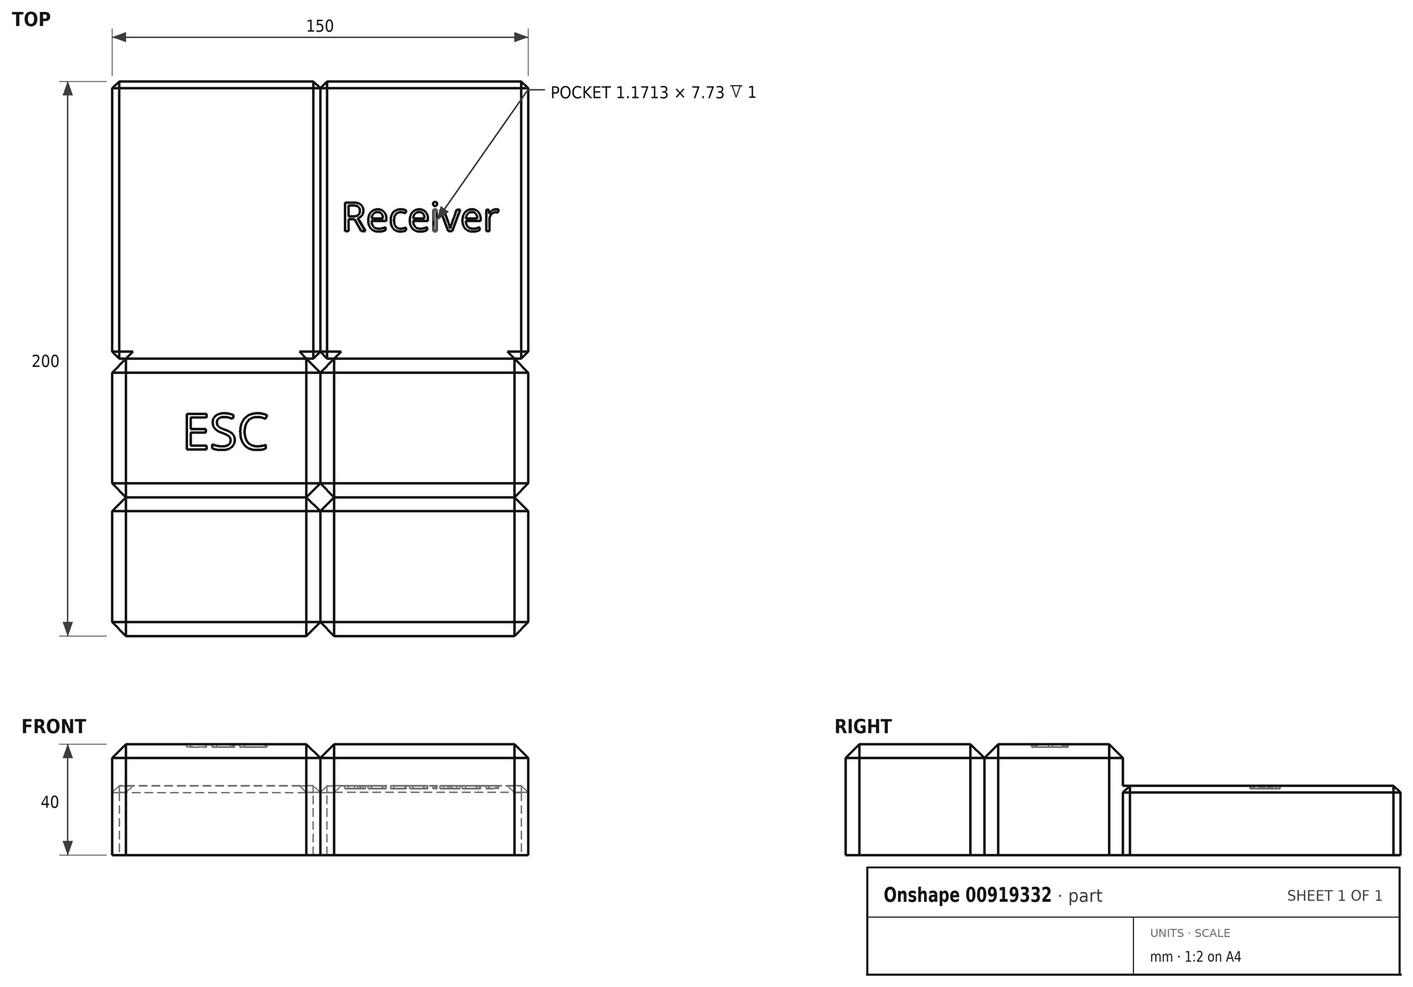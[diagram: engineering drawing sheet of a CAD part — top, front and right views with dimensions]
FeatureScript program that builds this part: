
annotation { "Feature Type Name" : "Feature", "Feature Type Description" : "" }
export const myFeature = defineFeature(function(context is Context, id is Id, definition is map)
    precondition{}
    {
        {
            var Q0;
            Q0=qCreatedBy(makeId("Top.planeOp"),FACE);
            var sketch = newSketch(context, id + "F0", { "sketchPlane" : qUnion([Q0])});
            skLineSegment(sketch, "E0.bottom", {"start": v(0, 0) * mm, "end": v(75, 0) * mm});
            skLineSegment(sketch, "E0.top", {"start": v(0, 50) * mm, "end": v(75, 50) * mm});
            skLineSegment(sketch, "E0.left", {"start": v(0, 0) * mm, "end": v(0, 50) * mm});
            skLineSegment(sketch, "E0.right", {"start": v(75, 0) * mm, "end": v(75, 50) * mm});
            skSolve(sketch);
        }
        {
            var Q0;
            Q0=makeQuery(id+"F0.imprint","IMPRINT",FACE,{"disambiguationData":[TD([[makeQuery(id+"F0.imprint","IMPRINT",EDGE,{"derivedFrom":sQuery(id+"F0.wireOp",EDGE,"E0.bottom")}),1.0]])]});
            extrude(context, id + "F1", {"entities" : qUnion([Q0]), "depth" : 40 * mm, "offsetDistance" : 25 * mm});
        }
        {
            var Q0;
            Q0=makeQuery(id+"F1.opExtrude","SWEPT_EDGE",EDGE,{"disambiguationData":[OSD([sQuery(id+"F0.wireOp",EDGE,"E0.bottom"),sQuery(id+"F0.wireOp",EDGE,"E0.left")])]});
            var Q1;
            Q1=makeQuery(id+"F1.opExtrude","SWEPT_EDGE",EDGE,{"disambiguationData":[OSD([sQuery(id+"F0.wireOp",EDGE,"E0.bottom"),sQuery(id+"F0.wireOp",EDGE,"E0.right")])]});
            var Q2;
            Q2=makeQuery(id+"F1.opExtrude","SWEPT_EDGE",EDGE,{"disambiguationData":[OSD([sQuery(id+"F0.wireOp",EDGE,"E0.top"),sQuery(id+"F0.wireOp",EDGE,"E0.right")])]});
            var Q3;
            Q3=makeQuery(id+"F1.opExtrude","SWEPT_EDGE",EDGE,{"disambiguationData":[OSD([sQuery(id+"F0.wireOp",EDGE,"E0.top"),sQuery(id+"F0.wireOp",EDGE,"E0.left")])]});
            var Q4;
            Q4=makeQuery(id+"F1.opExtrude","CAP_FACE",FACE,{"disambiguationData":[OSD([sQuery(id+"F0.wireOp",EDGE,"E0.bottom"),sQuery(id+"F0.wireOp",EDGE,"E0.top"),sQuery(id+"F0.wireOp",EDGE,"E0.left"),sQuery(id+"F0.wireOp",EDGE,"E0.right")])],"isStart":false});
            chamfer(context, id + "F2", {"entities" : qUnion([Q0, Q1, Q2, Q3, Q4]), "width" : 5 * mm, "tangentPropagation" : true});
        }
        {
            var Q0;
            Q0=makeQuery(id+"F1.opExtrude","SWEPT_BODY",BODY,{"disambiguationData":[OSD([sQuery(id+"F0.wireOp",EDGE,"E0.bottom"),sQuery(id+"F0.wireOp",EDGE,"E0.top"),sQuery(id+"F0.wireOp",EDGE,"E0.left"),sQuery(id+"F0.wireOp",EDGE,"E0.right")])]});
            var Q1;
            Q1=makeQuery(id+"F1.opExtrude","SWEPT_FACE",FACE,{"disambiguationData":[OSD([sQuery(id+"F0.wireOp",EDGE,"E0.top")])]});
            mirror(context, id + "F3", {"operationType" : NewBodyOperationType.ADD, "entities" : qUnion([Q0]), "mirrorPlane" : qUnion([Q1])});
        }
        {
            var Q0;
            {var subQ0=makeQuery(id+"F1.opExtrude","CAP_FACE",FACE,{"disambiguationData":[OSD([sQuery(id+"F0.wireOp",EDGE,"E0.bottom"),sQuery(id+"F0.wireOp",EDGE,"E0.top"),sQuery(id+"F0.wireOp",EDGE,"E0.left"),sQuery(id+"F0.wireOp",EDGE,"E0.right")])],"isStart":true});Q0=makeQuery(id+"F3.boolean.opBoolean","MERGE",FACE,{"derivedFrom":[subQ0,makeQuery(id+"F3.opPattern","COPY",FACE,{"derivedFrom":subQ0,"instanceName":"1"})]});}
            var sketch = newSketch(context, id + "F4", { "sketchPlane" : qUnion([Q0])});
            skLineSegment(sketch, "E1.bottom", {"start": v(0, -100) * mm, "end": v(75, -100) * mm});
            skLineSegment(sketch, "E1.top", {"start": v(0, -200) * mm, "end": v(75, -200) * mm});
            skLineSegment(sketch, "E1.left", {"start": v(0, -100) * mm, "end": v(0, -200) * mm});
            skLineSegment(sketch, "E1.right", {"start": v(75, -100) * mm, "end": v(75, -200) * mm});
            skSolve(sketch);
        }
        {
            var Q0;
            Q0=makeQuery(id+"F4.imprint","IMPRINT",FACE,{"disambiguationData":[TD([[makeQuery(id+"F4.imprint","IMPRINT",EDGE,{"derivedFrom":sQuery(id+"F4.wireOp",EDGE,"E1.top")}),1.0]])]});
            extrude(context, id + "F5", {"entities" : qUnion([Q0]), "operationType" : NewBodyOperationType.ADD, "oppositeDirection" : true, "depth" : 25 * mm, "offsetDistance" : 25 * mm});
        }
        {
            var Q0;
            Q0=makeQuery(id+"F5.opExtrude","SWEPT_EDGE",EDGE,{"disambiguationData":[OSD([sQuery(id+"F4.wireOp",EDGE,"E1.bottom"),sQuery(id+"F4.wireOp",EDGE,"E1.right")])]});
            var Q1;
            Q1=makeQuery(id+"F5.opExtrude","SWEPT_EDGE",EDGE,{"disambiguationData":[OSD([sQuery(id+"F4.wireOp",EDGE,"E1.top"),sQuery(id+"F4.wireOp",EDGE,"E1.right")])]});
            var Q2;
            Q2=makeQuery(id+"F5.opExtrude","SWEPT_EDGE",EDGE,{"disambiguationData":[OSD([sQuery(id+"F4.wireOp",EDGE,"E1.top"),sQuery(id+"F4.wireOp",EDGE,"E1.left")])]});
            var Q3;
            Q3=makeQuery(id+"F5.opExtrude","SWEPT_EDGE",EDGE,{"disambiguationData":[OSD([sQuery(id+"F4.wireOp",EDGE,"E1.bottom"),sQuery(id+"F4.wireOp",EDGE,"E1.left")])]});
            var Q4;
            Q4=makeQuery(id+"F5.opExtrude","CAP_EDGE",EDGE,{"disambiguationData":[OSD([sQuery(id+"F4.wireOp",EDGE,"E1.left")])],"isStart":false});
            var Q5;
            Q5=makeQuery(id+"F5.opExtrude","CAP_EDGE",EDGE,{"disambiguationData":[OSD([sQuery(id+"F4.wireOp",EDGE,"E1.right")])],"isStart":false});
            var Q6;
            Q6=makeQuery(id+"F5.opExtrude","CAP_EDGE",EDGE,{"disambiguationData":[OSD([sQuery(id+"F4.wireOp",EDGE,"E1.top")])],"isStart":false});
            var Q7;
            {var subQ0=sQuery(id+"F4.wireOp",EDGE,"E1.right");var subQ1=sQuery(id+"F4.wireOp",EDGE,"E1.bottom");var subQ2=makeQuery(id+"F5.opExtrude","CAP_FACE",FACE,{"disambiguationData":[OSD([subQ1,sQuery(id+"F4.wireOp",EDGE,"E1.top"),sQuery(id+"F4.wireOp",EDGE,"E1.left"),subQ0])],"isStart":false});var subQ3=makeQuery(id+"F5.opExtrude","SWEPT_FACE",FACE,{"disambiguationData":[OSD([subQ1])]});Q7=makeQuery(id+"F5.boolean.opBoolean","SPLIT",EDGE,{"disambiguationData":[topologyDisambiguationEdgeConnected([subQ3,subQ2]),TD([makeQuery(id+"F5.opExtrude","SWEPT_FACE",FACE,{"disambiguationData":[OSD([subQ0])]})])],"derivedFrom":makeQuery(id+"F5.opExtrude","CAP_EDGE",EDGE,{"disambiguationData":[OSD([subQ1])],"isStart":false})});}
            var Q8;
            {var subQ0=sQuery(id+"F4.wireOp",EDGE,"E1.left");var subQ1=sQuery(id+"F4.wireOp",EDGE,"E1.bottom");var subQ2=makeQuery(id+"F5.opExtrude","CAP_FACE",FACE,{"disambiguationData":[OSD([subQ1,sQuery(id+"F4.wireOp",EDGE,"E1.top"),subQ0,sQuery(id+"F4.wireOp",EDGE,"E1.right")])],"isStart":false});var subQ4=makeQuery(id+"F5.opExtrude","SWEPT_FACE",FACE,{"disambiguationData":[OSD([subQ1])]});Q8=makeQuery(id+"F5.boolean.opBoolean","SPLIT",EDGE,{"disambiguationData":[topologyDisambiguationEdgeConnected([subQ4,subQ2]),TD([makeQuery(id+"F5.opExtrude","SWEPT_FACE",FACE,{"disambiguationData":[OSD([subQ0])]})])],"derivedFrom":makeQuery(id+"F5.opExtrude","CAP_EDGE",EDGE,{"disambiguationData":[OSD([subQ1])],"isStart":false})});}
            chamfer(context, id + "F6", {"entities" : qUnion([Q0, Q1, Q2, Q3, Q4, Q5, Q6, Q7, Q8]), "width" : 2.5 * mm, "tangentPropagation" : true});
        }
        {
            var Q0;
            Q0=makeQuery(id+"F1.opExtrude","SWEPT_BODY",BODY,{"disambiguationData":[OSD([sQuery(id+"F0.wireOp",EDGE,"E0.bottom"),sQuery(id+"F0.wireOp",EDGE,"E0.top"),sQuery(id+"F0.wireOp",EDGE,"E0.left"),sQuery(id+"F0.wireOp",EDGE,"E0.right")])]});
            var Q1;
            Q1=makeQuery(id+"F5.opExtrude","SWEPT_FACE",FACE,{"disambiguationData":[OSD([sQuery(id+"F4.wireOp",EDGE,"E1.right")])]});
            mirror(context, id + "F7", {"operationType" : NewBodyOperationType.ADD, "entities" : qUnion([Q0]), "mirrorPlane" : qUnion([Q1])});
        }
        {
            var Q0;
            Q0=makeQuery(id+"F3.opPattern","COPY",FACE,{"derivedFrom":makeQuery(id+"F1.opExtrude","CAP_FACE",FACE,{"disambiguationData":[OSD([sQuery(id+"F0.wireOp",EDGE,"E0.bottom"),sQuery(id+"F0.wireOp",EDGE,"E0.top"),sQuery(id+"F0.wireOp",EDGE,"E0.left"),sQuery(id+"F0.wireOp",EDGE,"E0.right")])],"isStart":false}),"instanceName":"1"});
            var sketch = newSketch(context, id + "F8", { "sketchPlane" : qUnion([Q0])});
            skText(sketch, "E2", { "text": "ESC\n\n", "fontName": "OpenSans-Regular.ttf"});
            const initialGuessF8  = {"E2": [0.0251, 0.06725, 1, 0, 0.013]};
            skSetInitialGuess(sketch, initialGuessF8);
            skSolve(sketch);
        }
        {
            var Q0;
            Q0 = qSketchRegion(id + "F8", true);
            extrude(context, id + "F9", {"entities" : qUnion([Q0]), "operationType" : NewBodyOperationType.REMOVE, "oppositeDirection" : true, "depth" : 1 * mm, "offsetDistance" : 25 * mm});
        }
        {
            var Q0;
            Q0=makeQuery(id+"F7.opPattern","COPY",FACE,{"derivedFrom":makeQuery(id+"F5.opExtrude","CAP_FACE",FACE,{"disambiguationData":[OSD([sQuery(id+"F4.wireOp",EDGE,"E1.bottom"),sQuery(id+"F4.wireOp",EDGE,"E1.top"),sQuery(id+"F4.wireOp",EDGE,"E1.left"),sQuery(id+"F4.wireOp",EDGE,"E1.right")])],"isStart":false}),"instanceName":"1"});
            var sketch = newSketch(context, id + "F10", { "sketchPlane" : qUnion([Q0])});
            skText(sketch, "E3", { "text": "Reciever", "fontName": "OpenSans-Regular.ttf"});
            skText(sketch, "E4", { "text": "Receiver\n", "fontName": "OpenSans-Regular.ttf"});
            const initialGuessF10  = {"E3": [0.1524, 0.21849, 1, 0, 0.01], "E4": [0.08257, 0.146, 1, 0, 0.0104]};
            skSetInitialGuess(sketch, initialGuessF10);
            skSolve(sketch);
        }
        {
            var Q0;
            Q0 = qSketchRegion(id + "F10", true);
            extrude(context, id + "F11", {"entities" : qUnion([Q0]), "operationType" : NewBodyOperationType.REMOVE, "oppositeDirection" : true, "depth" : 1 * mm, "offsetDistance" : 25 * mm});
        }
    });
